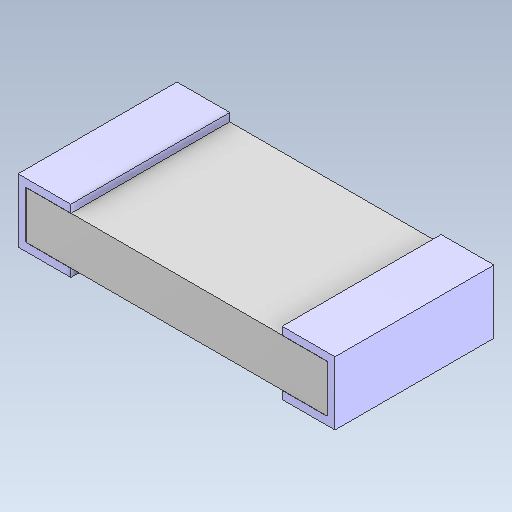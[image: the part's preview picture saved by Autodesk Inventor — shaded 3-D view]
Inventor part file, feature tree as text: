
AUTODESK INVENTOR PART (.ipt)
format: ipt  version: 2020 (Build 240168000, 168)  size: 108,032 bytes
history: native  units: mm
features: other x1, mirror x1
ambient origin geometry x8: Origin, YZ Plane, XZ Plane, XY Plane, X Axis, Y Axis, Z Axis, Center Point
bodies: Body1 (feature_tree)
feature tree (2):
  other  "Твердое тело1"
  mirror  "Mirror1"
